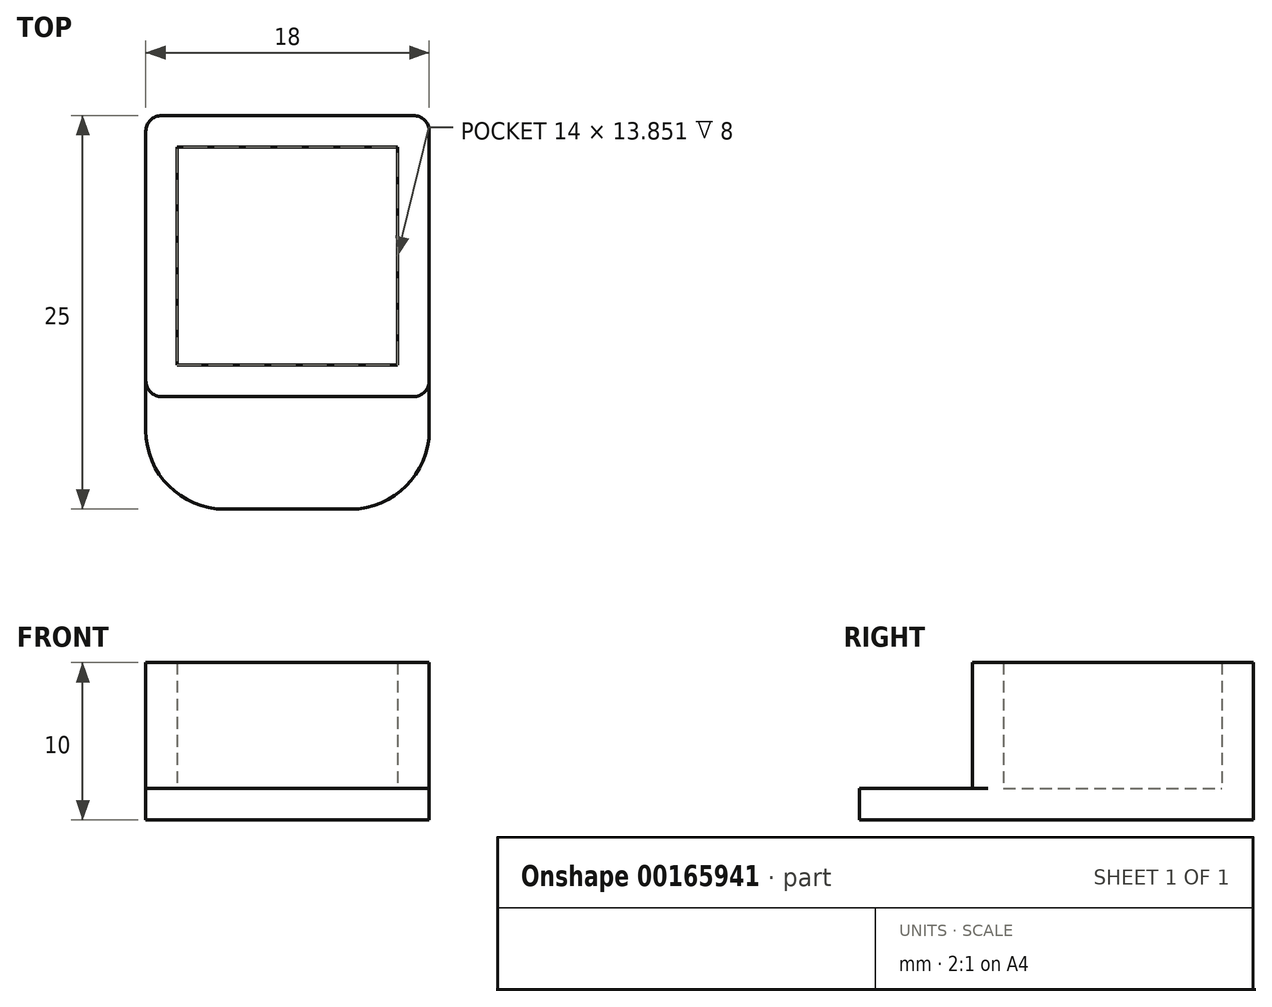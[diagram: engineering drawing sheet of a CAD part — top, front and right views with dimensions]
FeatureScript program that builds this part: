
annotation { "Feature Type Name" : "Feature", "Feature Type Description" : "" }
export const myFeature = defineFeature(function(context is Context, id is Id, definition is map)
    precondition{}
    {
        {
            var Q0;
            Q0=qCreatedBy(makeId("Top.planeOp"),FACE);
            var sketch = newSketch(context, id + "F0", { "sketchPlane" : qUnion([Q0])});
            skLineSegment(sketch, "E0.bottom", {"start": v(7, -6.93) * mm, "end": v(-7, -6.93) * mm});
            skLineSegment(sketch, "E0.top", {"start": v(7, 6.93) * mm, "end": v(-7, 6.93) * mm});
            skLineSegment(sketch, "E0.left", {"start": v(7, -6.93) * mm, "end": v(7, 6.93) * mm});
            skLineSegment(sketch, "E0.right", {"start": v(-7, -6.93) * mm, "end": v(-7, 6.93) * mm});
            skPoint(sketch, "E0.middle", {"position": v(0, 0) * mm});
            skLineSegment(sketch, "E1.bottom", {"start": v(9, -8.93) * mm, "end": v(-9, -8.93) * mm});
            skLineSegment(sketch, "E1.top", {"start": v(9, 8.93) * mm, "end": v(-9, 8.93) * mm});
            skLineSegment(sketch, "E1.left", {"start": v(9, -8.93) * mm, "end": v(9, 8.93) * mm});
            skLineSegment(sketch, "E1.right", {"start": v(-9, -8.93) * mm, "end": v(-9, 8.93) * mm});
            skSolve(sketch);
        }
        {
            var Q0;
            Q0 = qSketchRegion(id + "F0", true);
            extrude(context, id + "F1", {"entities" : qUnion([Q0]), "depth" : 10 * mm});
        }
        {
            var Q0;
            Q0=qCreatedBy(makeId("Top.planeOp"),FACE);
            var sketch = newSketch(context, id + "F2", { "sketchPlane" : qUnion([Q0])});
            skLineSegment(sketch, "E2.bottom", {"start": v(-9, 8.93) * mm, "end": v(9, 8.93) * mm});
            skLineSegment(sketch, "E2.top", {"start": v(-9, -16.07) * mm, "end": v(9, -16.07) * mm});
            skLineSegment(sketch, "E2.left", {"start": v(-9, 8.93) * mm, "end": v(-9, -16.07) * mm});
            skLineSegment(sketch, "E2.right", {"start": v(9, 8.93) * mm, "end": v(9, -16.07) * mm});
            skSolve(sketch);
        }
        {
            var Q0;
            Q0 = qSketchRegion(id + "F2", true);
            extrude(context, id + "F3", {"entities" : qUnion([Q0]), "operationType" : NewBodyOperationType.ADD, "depth" : 2 * mm});
        }
        {
            var Q0;
            Q0=makeQuery(id+"F3.opExtrude","SWEPT_EDGE",EDGE,{"disambiguationData":[OSD([sQuery(id+"F2.wireOp",EDGE,"E2.top"),sQuery(id+"F2.wireOp",EDGE,"E2.right")])]});
            var Q1;
            Q1=makeQuery(id+"F3.opExtrude","SWEPT_EDGE",EDGE,{"disambiguationData":[OSD([sQuery(id+"F2.wireOp",EDGE,"E2.top"),sQuery(id+"F2.wireOp",EDGE,"E2.left")])]});
            fillet(context, id + "F4", {"entities" : qUnion([Q0, Q1]), "radius" : 5 * mm, "tangentPropagation" : true, "allowEdgeOverflow" : false});
        }
        {
            var Q0;
            Q0=makeQuery(id+"F1.opExtrude","SWEPT_EDGE",EDGE,{"disambiguationData":[OSD([sQuery(id+"F0.wireOp",EDGE,"E1.bottom"),sQuery(id+"F0.wireOp",EDGE,"E1.left")])]});
            var Q1;
            Q1=makeQuery(id+"F1.opExtrude","SWEPT_EDGE",EDGE,{"disambiguationData":[OSD([sQuery(id+"F0.wireOp",EDGE,"E1.bottom"),sQuery(id+"F0.wireOp",EDGE,"E1.right")])]});
            var Q2;
            Q2=makeQuery(id+"F1.opExtrude","SWEPT_EDGE",EDGE,{"disambiguationData":[OSD([sQuery(id+"F0.wireOp",EDGE,"E1.top"),sQuery(id+"F0.wireOp",EDGE,"E1.right")])]});
            var Q3;
            Q3=makeQuery(id+"F1.opExtrude","SWEPT_EDGE",EDGE,{"disambiguationData":[OSD([sQuery(id+"F0.wireOp",EDGE,"E1.top"),sQuery(id+"F0.wireOp",EDGE,"E1.left")])]});
            fillet(context, id + "F5", {"entities" : qUnion([Q0, Q1, Q2, Q3]), "radius" : 1 * mm, "tangentPropagation" : true, "allowEdgeOverflow" : false});
        }
    });
